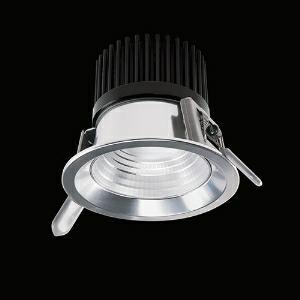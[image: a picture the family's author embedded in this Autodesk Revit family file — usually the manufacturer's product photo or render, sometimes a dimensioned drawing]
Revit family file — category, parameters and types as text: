
# Revit family: spectral_myral_myral_3500-840-s-dali
name_source: partatom
category: Lighting Fixtures
revit_build: Autodesk Revit 2016 (Build: 20150220_1215(x64)
units: mm (PartAtom-declared; Revit-internal decimal feet)

## family parameters
Cut with Voids When Loaded = No
Host = Face
Light Source = No
Part Type = Normal
Room Calculation Point = No
Round Connector Dimension = Use Diameter
Shared = No

## types (1)
- SPECTRAL MYRAL (1 x )
    Apparent Load = 0 VA
    Approval mark = CE
    CIE Flux Codes = 85 100 100 100 100
    Control Gear = Electronic transformer
    Default Elevation = 1800 mm
    Description = SPG0330175
MYRAL recessed spot

Design:
    Height = 0 mm  [stored 0 ft]
    Lamp = 1 x
    Lamp count = 1
    Length = 120 mm
    Luminous efficacy = 0 lm/W
    Manufacturer = Ridi
    ModVariant = No
    Model = MYRAL 3500-840-S-DALI
    Mounting Place = Ceiling
    Mounting Type = Recessed
    Number of Poles = 1
    OnlyDefault = Yes
    Power Factor = 1
    Product Name = SPECTRAL MYRAL
    Product group = Downlight recessed
    ProductGroupID = 400
    Protection Class = Protection class
    Protection Degree = IP 20
    RlxData = <blob elided: 38925 chars, md5=4e31a9f5>
    Socket = socket
    Standby Power = 0 W
    System Light Flux = 0 lm
    System Power = 0 W
    Type Image = myral_04.jpg
    URL = http://reluxnet.relux.com
    VarID = ---
    Voltage = 0 V
    Weight = 0.00 kg
    Width = 0 mm  [stored 0 ft]

note: [stored X ft] marks values corroborated as IEEE doubles in the binary element streams (Revit-internal decimal feet)

## geometry (parser evidence)
native form markers: Sweep x12
no freeform markers — native parametric forms only
